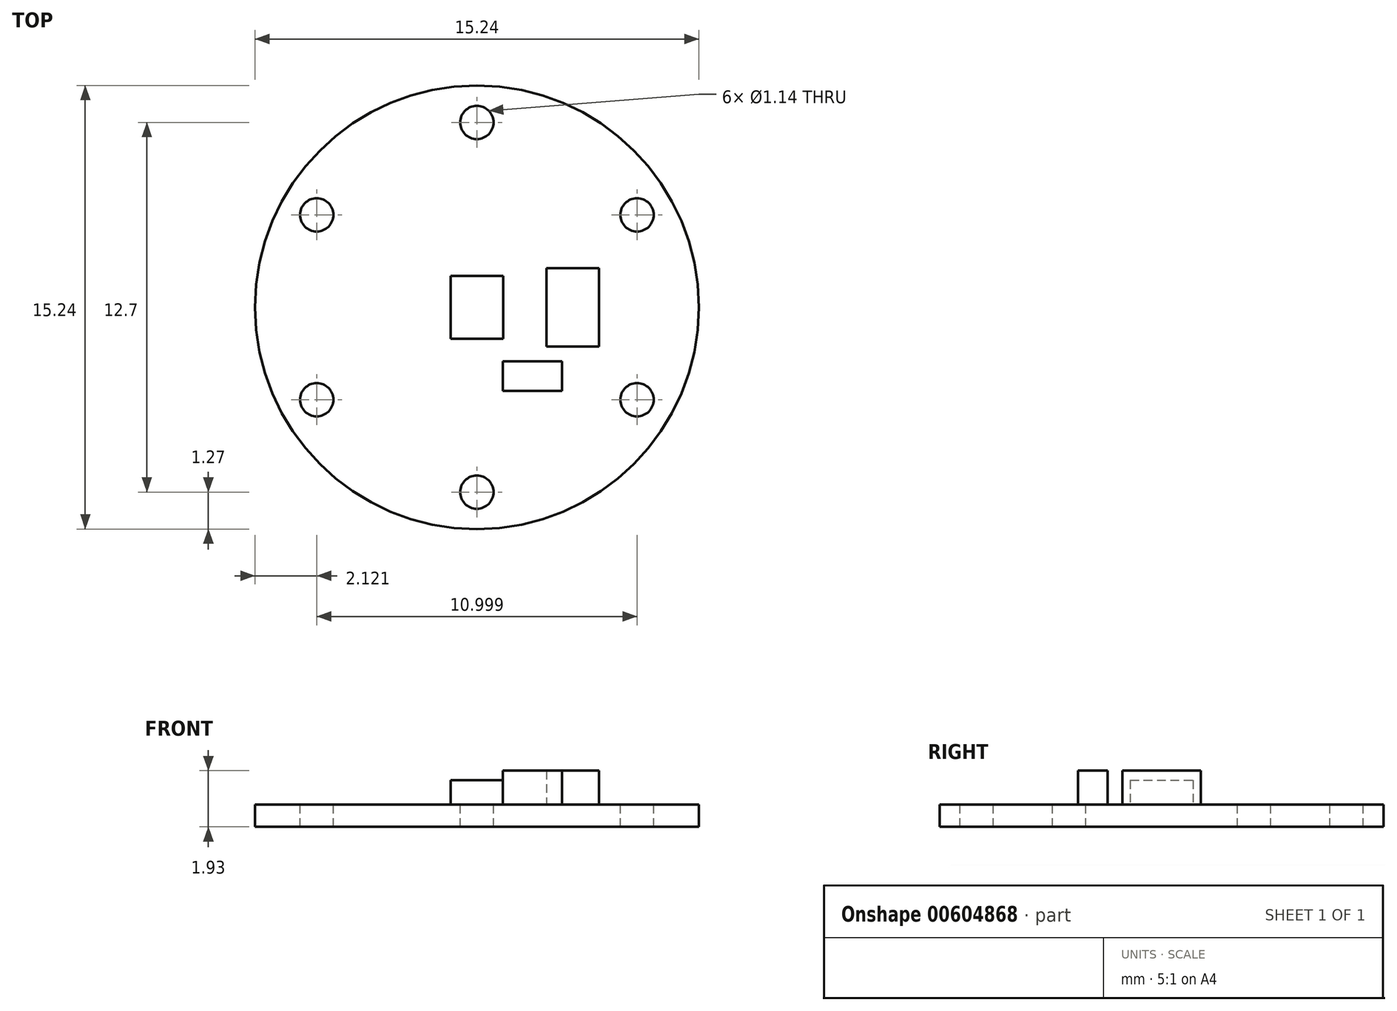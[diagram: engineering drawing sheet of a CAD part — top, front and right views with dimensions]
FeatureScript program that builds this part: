
annotation { "Feature Type Name" : "Feature", "Feature Type Description" : "" }
export const myFeature = defineFeature(function(context is Context, id is Id, definition is map)
    precondition{}
    {
        {
            var Q0;
            Q0=qCreatedBy(makeId("Top.planeOp"),FACE);
            var sketch = newSketch(context, id + "F0", { "sketchPlane" : qUnion([Q0])});
            skCircle(sketch, "E0", {"center": v(0, 0) * mm, "radius": 7.62 * mm});
            skSolve(sketch);
        }
        {
            var Q0;
            Q0 = qSketchRegion(id + "F0", true);
            extrude(context, id + "F1", {"entities" : qUnion([Q0]), "depth" : 0.76 * mm, "offsetDistance" : 25.4 * mm});
        }
        {
            var Q0;
            Q0=makeQuery(id+"F1.opExtrude","CAP_FACE",FACE,{"disambiguationData":[OSD([sQuery(id+"F0.wireOp",EDGE,"E0")])],"isStart":false});
            var sketch = newSketch(context, id + "F2", { "sketchPlane" : qUnion([Q0])});
            skCircle(sketch, "E1", {"center": v(0, 6.35) * mm, "radius": 0.57 * mm});
            skLineSegment(sketch, "E2", {"start": v(-7.62, 0) * mm, "end": v(0, 0) * mm, "construction": true});
            skCircle(sketch, "E3.1.0", {"center": v(-5.5, 3.18) * mm, "radius": 0.57 * mm});
            skCircle(sketch, "E3.2.0", {"center": v(-5.5, -3.17) * mm, "radius": 0.57 * mm});
            skCircle(sketch, "E3.3.0", {"center": v(0, -6.35) * mm, "radius": 0.57 * mm});
            skCircle(sketch, "E3.4.0", {"center": v(5.5, -3.18) * mm, "radius": 0.57 * mm});
            skCircle(sketch, "E3.5.0", {"center": v(5.5, 3.18) * mm, "radius": 0.57 * mm});
            skPoint(sketch, "E3.center", {"position": v(0, 0) * mm});
            skSolve(sketch);
        }
        {
            var Q0;
            Q0 = qSketchRegion(id + "F2", true);
            extrude(context, id + "F3", {"entities" : qUnion([Q0]), "operationType" : NewBodyOperationType.REMOVE, "endBound" : BoundingType.UP_TO_NEXT, "oppositeDirection" : true, "depth" : 25.4 * mm, "offsetDistance" : 25.4 * mm});
        }
        {
            var Q0;
            Q0=makeQuery(id+"F1.opExtrude","CAP_FACE",FACE,{"disambiguationData":[OSD([sQuery(id+"F0.wireOp",EDGE,"E0")])],"isStart":true});
            var sketch = newSketch(context, id + "F4", { "sketchPlane" : qUnion([Q0])});
            skLineSegment(sketch, "E4.bottom", {"start": v(-0.9, 1.08) * mm, "end": v(0.9, 1.08) * mm});
            skLineSegment(sketch, "E4.top", {"start": v(-0.9, -1.08) * mm, "end": v(0.9, -1.08) * mm});
            skLineSegment(sketch, "E4.left", {"start": v(-0.9, 1.08) * mm, "end": v(-0.9, -1.08) * mm});
            skLineSegment(sketch, "E4.right", {"start": v(0.9, 1.08) * mm, "end": v(0.9, -1.08) * mm});
            skLineSegment(sketch, "E5", {"start": v(0.9, 1.08) * mm, "end": v(-0.9, -1.08) * mm, "construction": true});
            skSolve(sketch);
        }
        {
            var Q0;
            Q0 = qSketchRegion(id + "F4", true);
            extrude(context, id + "F5", {"entities" : qUnion([Q0]), "operationType" : NewBodyOperationType.ADD, "oppositeDirection" : true, "depth" : 1.6 * mm, "offsetDistance" : 25.4 * mm});
        }
        {
            var Q0;
            Q0=makeQuery(id+"F1.opExtrude","CAP_FACE",FACE,{"disambiguationData":[OSD([sQuery(id+"F0.wireOp",EDGE,"E0")])],"isStart":true});
            var sketch = newSketch(context, id + "F6", { "sketchPlane" : qUnion([Q0])});
            skLineSegment(sketch, "E6.bottom", {"start": v(0.89, 2.87) * mm, "end": v(2.92, 2.87) * mm});
            skLineSegment(sketch, "E6.top", {"start": v(0.89, 1.85) * mm, "end": v(2.92, 1.85) * mm});
            skLineSegment(sketch, "E6.left", {"start": v(0.89, 2.87) * mm, "end": v(0.89, 1.85) * mm});
            skLineSegment(sketch, "E6.right", {"start": v(2.92, 2.87) * mm, "end": v(2.92, 1.85) * mm});
            skLineSegment(sketch, "E7.bottom", {"start": v(2.39, 1.35) * mm, "end": v(4.2, 1.35) * mm});
            skLineSegment(sketch, "E7.top", {"start": v(2.39, -1.35) * mm, "end": v(4.2, -1.35) * mm});
            skLineSegment(sketch, "E7.left", {"start": v(2.39, 1.35) * mm, "end": v(2.39, -1.35) * mm});
            skLineSegment(sketch, "E7.right", {"start": v(4.2, 1.35) * mm, "end": v(4.2, -1.35) * mm});
            skLineSegment(sketch, "E8", {"start": v(0, 0) * mm, "end": v(7.62, 0) * mm, "construction": true});
            skSolve(sketch);
        }
        {
            var Q0;
            Q0 = qSketchRegion(id + "F6", true);
            extrude(context, id + "F7", {"entities" : qUnion([Q0]), "operationType" : NewBodyOperationType.ADD, "oppositeDirection" : true, "depth" : 1.93 * mm, "offsetDistance" : 25.4 * mm});
        }
    });
